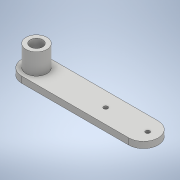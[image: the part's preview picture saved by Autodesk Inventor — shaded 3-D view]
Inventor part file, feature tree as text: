
AUTODESK INVENTOR PART (.ipt)
format: ipt  version: 2020 (Build 240168000, 168)  size: 123,904 bytes
history: native  units: mm
features: sketch x3, extrude x2, other x1, hole x1
ambient origin geometry x8: Origin, YZ Plane, XZ Plane, XY Plane, X Axis, Y Axis, Z Axis, Center Point
bodies: Body1 (feature_tree)
feature tree (7):
  other  "Твердое тело1"
  extrude  "Выдавливание1"  Depth=25.5mm
  extrude  "Выдавливание2"  Depth=7.0mm
  hole  "Отверстие1"  [1 undecoded]
  sketch  "Эскиз1"
  sketch  "Эскиз2"
  sketch  "Эскиз6"
note: 1 required parameter value undecoded (feature->parameter linkage not recoverable at this tier; creation-order binding heuristic only, values carry confidence <= 0.55)
